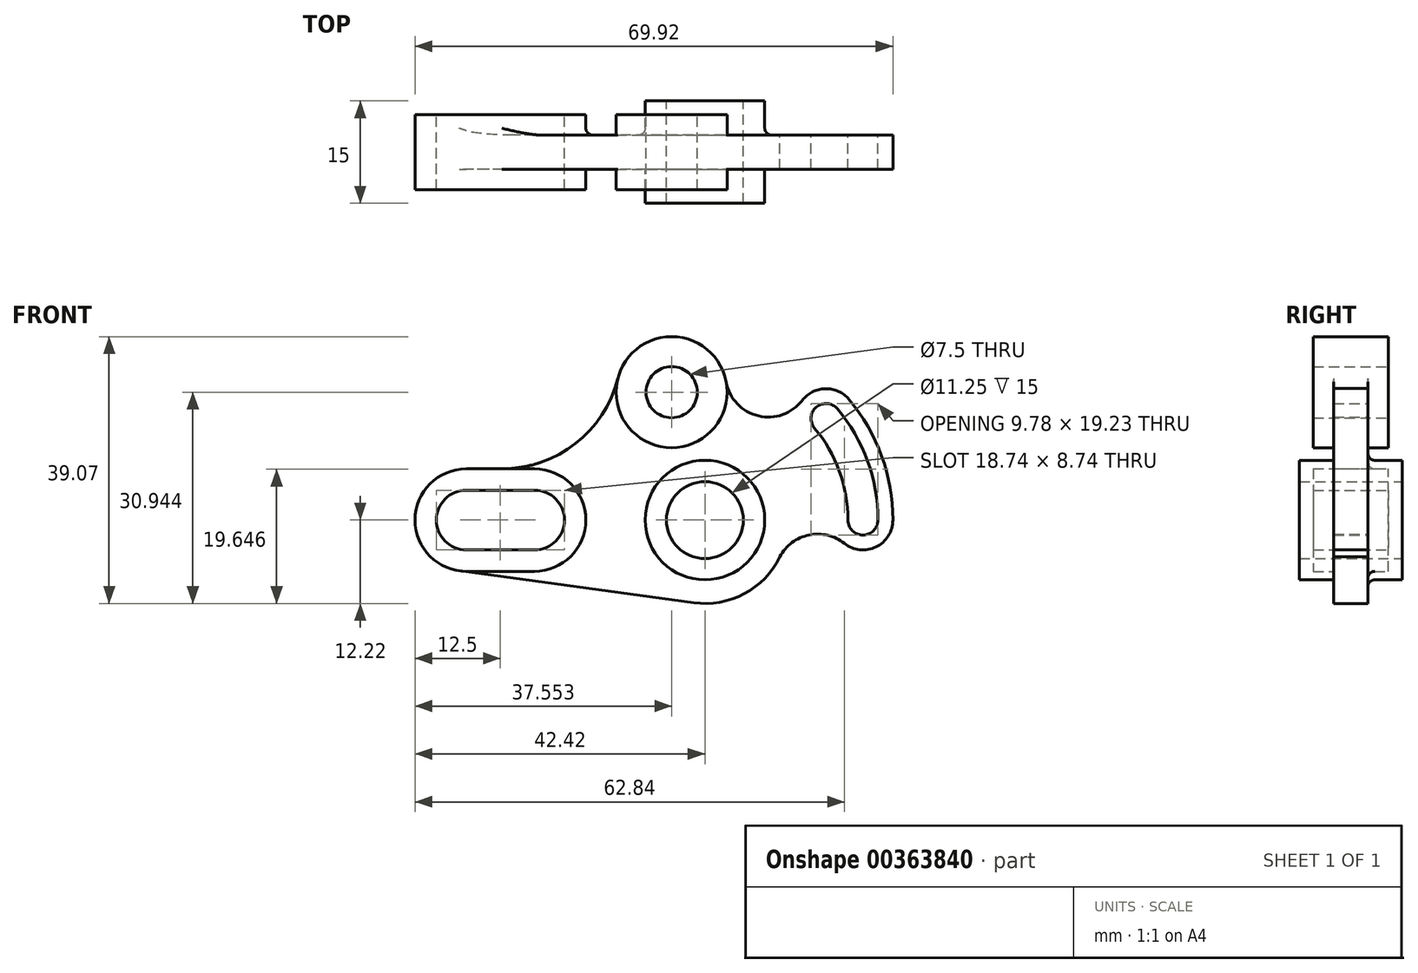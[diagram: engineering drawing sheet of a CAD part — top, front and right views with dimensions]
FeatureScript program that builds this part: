
annotation { "Feature Type Name" : "Feature", "Feature Type Description" : "" }
export const myFeature = defineFeature(function(context is Context, id is Id, definition is map)
    precondition{}
    {
        {
            var Q0;
            Q0=qCreatedBy(makeId("Front.planeOp"),FACE);
            var sketch = newSketch(context, id + "F0", { "sketchPlane" : qUnion([Q0])});
            skCircle(sketch, "E0", {"center": v(0, 0) * mm, "radius": 5.62 * mm});
            skCircle(sketch, "E1", {"center": v(0, 0) * mm, "radius": 8.75 * mm});
            skLineSegment(sketch, "E2", {"start": v(0, 0) * mm, "end": v(23.12, 0) * mm, "construction": true});
            skLineSegment(sketch, "E3", {"start": v(23.12, 0) * mm, "end": v(-34.92, 0) * mm, "construction": true});
            skLineSegment(sketch, "E4", {"start": v(-34.92, 0) * mm, "end": v(-24.92, 0) * mm, "construction": true});
            skArc(sketch, "E5", {"start": v(-24.92, -4.37) * mm, "mid": v(-20.55, 0) * mm, "end": v(-24.92, 4.37) * mm});
            skArc(sketch, "E6", {"start": v(-34.92, 4.37) * mm, "mid": v(-39.3, 0) * mm, "end": v(-34.92, -4.37) * mm});
            skLineSegment(sketch, "E7", {"start": v(-34.92, 4.37) * mm, "end": v(-24.92, 4.37) * mm});
            skLineSegment(sketch, "E8", {"start": v(-34.92, -4.37) * mm, "end": v(-24.92, -4.37) * mm});
            skArc(sketch, "E9", {"start": v(-34.92, 7.5) * mm, "mid": v(-42.42, 0) * mm, "end": v(-34.92, -7.5) * mm});
            skArc(sketch, "E10", {"start": v(-24.92, -7.5) * mm, "mid": v(-17.42, 0) * mm, "end": v(-24.92, 7.5) * mm});
            skLineSegment(sketch, "E11", {"start": v(-34.92, 7.5) * mm, "end": v(-24.92, 7.5) * mm});
            skLineSegment(sketch, "E12", {"start": v(-24.92, -7.5) * mm, "end": v(-34.92, -7.5) * mm});
            skArc(sketch, "E13", {"start": v(20.93, 0) * mm, "mid": v(23.12, -2.19) * mm, "end": v(25.31, 0) * mm});
            skArc(sketch, "E14", {"start": v(20.38, -3.41) * mm, "mid": v(25.01, -3.94) * mm, "end": v(27.5, 0) * mm});
            skLineSegment(sketch, "E15", {"start": v(0, 0) * mm, "end": v(17.71, 14.86) * mm, "construction": true});
            skArc(sketch, "E16", {"start": v(19.39, 16.27) * mm, "mid": v(16.3, 16.54) * mm, "end": v(16.03, 13.45) * mm});
            skArc(sketch, "E17", {"start": v(21.06, 17.67) * mm, "mid": v(17.61, 19.24) * mm, "end": v(14.24, 17.52) * mm});
            skCircle(sketch, "E18", {"center": v(-4.87, 18.72) * mm, "radius": 3.75 * mm});
            skCircle(sketch, "E19", {"center": v(-4.87, 18.72) * mm, "radius": 8.12 * mm});
            skArc(sketch, "E20", {"start": v(21.06, 17.67) * mm, "mid": v(25.84, 9.4) * mm, "end": v(27.5, 0) * mm});
            skArc(sketch, "E21", {"start": v(3.12, 20.19) * mm, "mid": v(7.81, 15.24) * mm, "end": v(14.24, 17.52) * mm});
            skArc(sketch, "E22", {"start": v(-29.71, 7.5) * mm, "mid": v(-18.96, 11.2) * mm, "end": v(-12.74, 20.71) * mm});
            skArc(sketch, "E23", {"start": v(-1.65, -12.1) * mm, "mid": v(5.75, -10.78) * mm, "end": v(10.97, -5.37) * mm});
            skArc(sketch, "E24", {"start": v(20.4, -3.43) * mm, "mid": v(15.23, -2.18) * mm, "end": v(10.97, -5.37) * mm});
            skLineSegment(sketch, "E25", {"start": v(-1.65, -12.1) * mm, "end": v(-35.93, -7.43) * mm});
            skArc(sketch, "E26", {"start": v(19.39, 16.27) * mm, "mid": v(23.78, 8.66) * mm, "end": v(25.3, 0) * mm});
            skArc(sketch, "E27", {"start": v(16.03, 13.45) * mm, "mid": v(19.67, 7.16) * mm, "end": v(20.93, 0) * mm});
            skSolve(sketch);
        }
        {
            var Q0;
            Q0=makeQuery(id+"F0.imprint","IMPRINT",FACE,{"disambiguationData":[TD([[makeQuery(id+"F0.imprint","IMPRINT",EDGE,{"derivedFrom":sQuery(id+"F0.wireOp",EDGE,"E1")}),-1.0]])]});
            extrude(context, id + "F1", {"entities" : qUnion([Q0]), "depth" : 5 * mm});
        }
        {
            var Q0;
            Q0=makeQuery(id+"F0.imprint","IMPRINT",FACE,{"disambiguationData":[TD([[makeQuery(id+"F0.imprint","IMPRINT",EDGE,{"derivedFrom":sQuery(id+"F0.wireOp",EDGE,"E5")}),-1.0]])]});
            var Q1;
            Q1=makeQuery(id+"F0.imprint","IMPRINT",FACE,{"disambiguationData":[TD([[makeQuery(id+"F0.imprint","IMPRINT",EDGE,{"derivedFrom":sQuery(id+"F0.wireOp",EDGE,"E18")}),-1.0]])]});
            extrude(context, id + "F2", {"entities" : qUnion([Q0, Q1]), "operationType" : NewBodyOperationType.ADD, "depth" : 8 * mm, "hasSecondDirection" : true, "secondDirectionOppositeDirection" : true, "secondDirectionDepth" : 3 * mm});
        }
        {
            var Q0;
            Q0=makeQuery(id+"F0.imprint","IMPRINT",FACE,{"disambiguationData":[TD([[makeQuery(id+"F0.imprint","IMPRINT",EDGE,{"derivedFrom":sQuery(id+"F0.wireOp",EDGE,"E0")}),-1.0]])]});
            extrude(context, id + "F3", {"entities" : qUnion([Q0]), "operationType" : NewBodyOperationType.ADD, "depth" : 10 * mm, "hasSecondDirection" : true, "secondDirectionOppositeDirection" : true, "secondDirectionDepth" : 5 * mm});
        }
        {
            var Q0;
            Q0=makeQuery(id+"F1.opExtrude","CAP_EDGE",EDGE,{"disambiguationData":[OSD([sQuery(id+"F0.wireOp",EDGE,"E10")])],"isStart":false});
            var Q1;
            Q1=makeQuery(id+"F1.opExtrude","CAP_EDGE",EDGE,{"disambiguationData":[OSD([sQuery(id+"F0.wireOp",EDGE,"E1")])],"isStart":false});
            var Q2;
            Q2=makeQuery(id+"F1.opExtrude","CAP_EDGE",EDGE,{"disambiguationData":[OSD([sQuery(id+"F0.wireOp",EDGE,"E19")])],"isStart":false});
            var Q3;
            Q3=makeQuery(id+"F1.opExtrude","CAP_EDGE",EDGE,{"disambiguationData":[OSD([sQuery(id+"F0.wireOp",EDGE,"E10")])],"isStart":true});
            var Q4;
            Q4=makeQuery(id+"F1.opExtrude","CAP_EDGE",EDGE,{"disambiguationData":[OSD([sQuery(id+"F0.wireOp",EDGE,"E1")])],"isStart":true});
            var Q5;
            Q5=makeQuery(id+"F1.opExtrude","CAP_EDGE",EDGE,{"disambiguationData":[OSD([sQuery(id+"F0.wireOp",EDGE,"E19")])],"isStart":true});
            fillet(context, id + "F4", {"entities" : qUnion([Q0, Q1, Q2, Q3, Q4, Q5]), "radius" : 1 * mm, "tangentPropagation" : true, "allowEdgeOverflow" : false});
        }
    });
